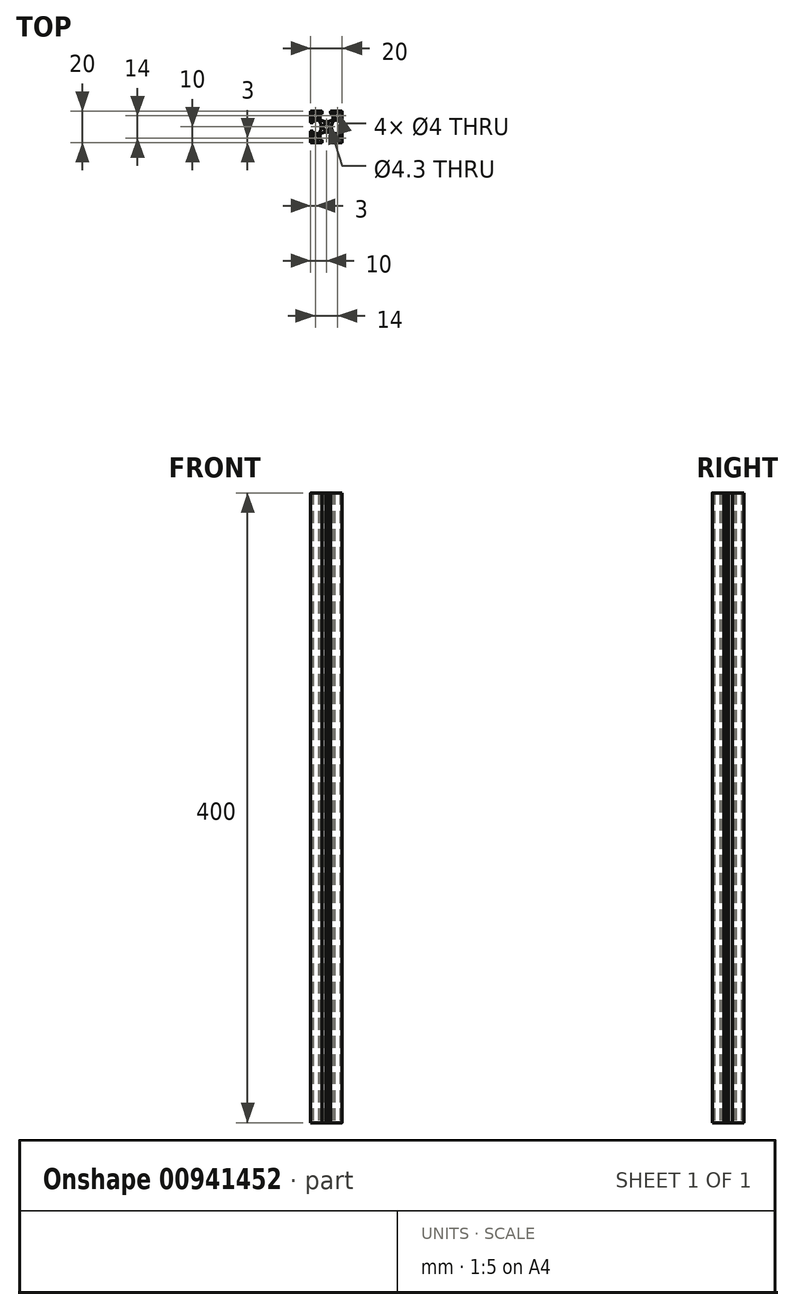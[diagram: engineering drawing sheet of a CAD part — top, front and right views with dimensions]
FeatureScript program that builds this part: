
annotation { "Feature Type Name" : "Feature", "Feature Type Description" : "" }
export const myFeature = defineFeature(function(context is Context, id is Id, definition is map)
    precondition{}
    {
        {
            var Q0;
            Q0=qCreatedBy(makeId("Top.planeOp"),FACE);
            var sketch = newSketch(context, id + "F0", { "sketchPlane" : qUnion([Q0])});
            skLineSegment(sketch, "E0", {"start": v(-11.2, 0) * mm, "end": v(11.2, 0) * mm});
            skCircle(sketch, "E1", {"center": v(0, 0) * mm, "radius": 2.15 * mm});
            skLineSegment(sketch, "E2", {"start": v(4.15, 4.94) * mm, "end": v(4.15, 8.2) * mm});
            skArc(sketch, "E3", {"start": v(4.15, 8.2) * mm, "mid": v(4.06, 8.41) * mm, "end": v(3.85, 8.5) * mm});
            skLineSegment(sketch, "E4", {"start": v(3.85, 8.5) * mm, "end": v(2.95, 8.5) * mm});
            skArc(sketch, "E5", {"start": v(2.95, 8.5) * mm, "mid": v(2.74, 8.59) * mm, "end": v(2.65, 8.8) * mm});
            skLineSegment(sketch, "E6", {"start": v(2.65, 8.8) * mm, "end": v(2.65, 9.7) * mm});
            skArc(sketch, "E7", {"start": v(2.65, 9.7) * mm, "mid": v(2.74, 9.91) * mm, "end": v(2.95, 10) * mm});
            skLineSegment(sketch, "E8", {"start": v(2.95, 10) * mm, "end": v(9.7, 10) * mm});
            skArc(sketch, "E9", {"start": v(9.7, 10) * mm, "mid": v(9.91, 9.91) * mm, "end": v(10, 9.7) * mm});
            skLineSegment(sketch, "E10", {"start": v(10, 9.7) * mm, "end": v(10, 2.95) * mm});
            skArc(sketch, "E11", {"start": v(10, 2.95) * mm, "mid": v(9.91, 2.74) * mm, "end": v(9.7, 2.65) * mm});
            skLineSegment(sketch, "E12", {"start": v(9.7, 2.65) * mm, "end": v(8.8, 2.65) * mm});
            skArc(sketch, "E13", {"start": v(8.8, 2.65) * mm, "mid": v(8.59, 2.74) * mm, "end": v(8.5, 2.95) * mm});
            skLineSegment(sketch, "E14", {"start": v(8.5, 2.95) * mm, "end": v(8.5, 3.85) * mm});
            skArc(sketch, "E15", {"start": v(8.5, 3.85) * mm, "mid": v(8.41, 4.06) * mm, "end": v(8.2, 4.15) * mm});
            skLineSegment(sketch, "E16", {"start": v(8.2, 4.15) * mm, "end": v(4.94, 4.15) * mm});
            skArc(sketch, "E17", {"start": v(4.94, 4.15) * mm, "mid": v(4.81, 4.12) * mm, "end": v(4.7, 4.04) * mm});
            skArc(sketch, "E18", {"start": v(4.7, 4.04) * mm, "mid": v(3.71, 2.28) * mm, "end": v(3.3, 0.3) * mm});
            skLineSegment(sketch, "E19", {"start": v(3.3, 0.3) * mm, "end": v(3, 0) * mm});
            skLineSegment(sketch, "E20", {"start": v(3, 0) * mm, "end": v(3.3, -0.3) * mm});
            skArc(sketch, "E21", {"start": v(3.3, -0.3) * mm, "mid": v(3.71, -2.28) * mm, "end": v(4.7, -4.04) * mm});
            skArc(sketch, "E22", {"start": v(4.7, -4.04) * mm, "mid": v(4.81, -4.12) * mm, "end": v(4.94, -4.15) * mm});
            skLineSegment(sketch, "E23", {"start": v(4.94, -4.15) * mm, "end": v(8.2, -4.15) * mm});
            skArc(sketch, "E24", {"start": v(8.2, -4.15) * mm, "mid": v(8.41, -4.06) * mm, "end": v(8.5, -3.85) * mm});
            skLineSegment(sketch, "E25", {"start": v(8.5, -3.85) * mm, "end": v(8.5, -2.95) * mm});
            skArc(sketch, "E26", {"start": v(8.5, -2.95) * mm, "mid": v(8.59, -2.74) * mm, "end": v(8.8, -2.65) * mm});
            skLineSegment(sketch, "E27", {"start": v(8.8, -2.65) * mm, "end": v(9.7, -2.65) * mm});
            skArc(sketch, "E28", {"start": v(9.7, -2.65) * mm, "mid": v(9.91, -2.74) * mm, "end": v(10, -2.95) * mm});
            skLineSegment(sketch, "E29", {"start": v(10, -2.95) * mm, "end": v(10, -9.7) * mm});
            skArc(sketch, "E30", {"start": v(10, -9.7) * mm, "mid": v(9.91, -9.91) * mm, "end": v(9.7, -10) * mm});
            skLineSegment(sketch, "E31", {"start": v(9.7, -10) * mm, "end": v(2.95, -10) * mm});
            skArc(sketch, "E32", {"start": v(2.95, -10) * mm, "mid": v(2.74, -9.91) * mm, "end": v(2.65, -9.7) * mm});
            skLineSegment(sketch, "E33", {"start": v(2.65, -9.7) * mm, "end": v(2.65, -8.8) * mm});
            skArc(sketch, "E34", {"start": v(2.65, -8.8) * mm, "mid": v(2.74, -8.59) * mm, "end": v(2.95, -8.5) * mm});
            skLineSegment(sketch, "E35", {"start": v(2.95, -8.5) * mm, "end": v(3.85, -8.5) * mm});
            skArc(sketch, "E36", {"start": v(3.85, -8.5) * mm, "mid": v(4.06, -8.41) * mm, "end": v(4.15, -8.2) * mm});
            skLineSegment(sketch, "E37", {"start": v(4.15, -8.2) * mm, "end": v(4.15, -4.94) * mm});
            skArc(sketch, "E38", {"start": v(4.15, -4.94) * mm, "mid": v(4.12, -4.81) * mm, "end": v(4.04, -4.7) * mm});
            skArc(sketch, "E39", {"start": v(4.04, -4.7) * mm, "mid": v(2.28, -3.71) * mm, "end": v(0.3, -3.3) * mm});
            skLineSegment(sketch, "E40", {"start": v(0.3, -3.3) * mm, "end": v(0, -3) * mm});
            skLineSegment(sketch, "E41", {"start": v(0, -3) * mm, "end": v(-0.3, -3.3) * mm});
            skArc(sketch, "E42", {"start": v(-0.3, -3.3) * mm, "mid": v(-2.28, -3.71) * mm, "end": v(-4.04, -4.7) * mm});
            skArc(sketch, "E43", {"start": v(-4.04, -4.7) * mm, "mid": v(-4.12, -4.81) * mm, "end": v(-4.15, -4.94) * mm});
            skLineSegment(sketch, "E44", {"start": v(-4.15, -4.94) * mm, "end": v(-4.15, -8.2) * mm});
            skArc(sketch, "E45", {"start": v(-4.15, -8.2) * mm, "mid": v(-4.06, -8.41) * mm, "end": v(-3.85, -8.5) * mm});
            skLineSegment(sketch, "E46", {"start": v(-3.85, -8.5) * mm, "end": v(-2.95, -8.5) * mm});
            skArc(sketch, "E47", {"start": v(-2.95, -8.5) * mm, "mid": v(-2.74, -8.59) * mm, "end": v(-2.65, -8.8) * mm});
            skLineSegment(sketch, "E48", {"start": v(-2.65, -8.8) * mm, "end": v(-2.65, -9.7) * mm});
            skArc(sketch, "E49", {"start": v(-2.65, -9.7) * mm, "mid": v(-2.74, -9.91) * mm, "end": v(-2.95, -10) * mm});
            skLineSegment(sketch, "E50", {"start": v(-2.95, -10) * mm, "end": v(-9.7, -10) * mm});
            skArc(sketch, "E51", {"start": v(-9.7, -10) * mm, "mid": v(-9.91, -9.91) * mm, "end": v(-10, -9.7) * mm});
            skLineSegment(sketch, "E52", {"start": v(-10, -9.7) * mm, "end": v(-10, -2.95) * mm});
            skArc(sketch, "E53", {"start": v(-10, -2.95) * mm, "mid": v(-9.91, -2.74) * mm, "end": v(-9.7, -2.65) * mm});
            skLineSegment(sketch, "E54", {"start": v(-9.7, -2.65) * mm, "end": v(-8.8, -2.65) * mm});
            skArc(sketch, "E55", {"start": v(-8.8, -2.65) * mm, "mid": v(-8.59, -2.74) * mm, "end": v(-8.5, -2.95) * mm});
            skLineSegment(sketch, "E56", {"start": v(-8.5, -2.95) * mm, "end": v(-8.5, -3.85) * mm});
            skArc(sketch, "E57", {"start": v(-8.5, -3.85) * mm, "mid": v(-8.41, -4.06) * mm, "end": v(-8.2, -4.15) * mm});
            skLineSegment(sketch, "E58", {"start": v(-8.2, -4.15) * mm, "end": v(-4.94, -4.15) * mm});
            skArc(sketch, "E59", {"start": v(-4.94, -4.15) * mm, "mid": v(-4.81, -4.12) * mm, "end": v(-4.7, -4.04) * mm});
            skArc(sketch, "E60", {"start": v(-4.7, -4.04) * mm, "mid": v(-3.71, -2.28) * mm, "end": v(-3.3, -0.3) * mm});
            skLineSegment(sketch, "E61", {"start": v(-3.3, -0.3) * mm, "end": v(-3, 0) * mm});
            skLineSegment(sketch, "E62", {"start": v(-3, 0) * mm, "end": v(-3.3, 0.3) * mm});
            skArc(sketch, "E63", {"start": v(-3.3, 0.3) * mm, "mid": v(-3.71, 2.28) * mm, "end": v(-4.7, 4.04) * mm});
            skArc(sketch, "E64", {"start": v(-4.7, 4.04) * mm, "mid": v(-4.81, 4.12) * mm, "end": v(-4.94, 4.15) * mm});
            skLineSegment(sketch, "E65", {"start": v(-4.94, 4.15) * mm, "end": v(-8.2, 4.15) * mm});
            skArc(sketch, "E66", {"start": v(-8.2, 4.15) * mm, "mid": v(-8.41, 4.06) * mm, "end": v(-8.5, 3.85) * mm});
            skLineSegment(sketch, "E67", {"start": v(-8.5, 3.85) * mm, "end": v(-8.5, 2.95) * mm});
            skArc(sketch, "E68", {"start": v(-8.5, 2.95) * mm, "mid": v(-8.59, 2.74) * mm, "end": v(-8.8, 2.65) * mm});
            skLineSegment(sketch, "E69", {"start": v(-8.8, 2.65) * mm, "end": v(-9.7, 2.65) * mm});
            skArc(sketch, "E70", {"start": v(-9.7, 2.65) * mm, "mid": v(-9.91, 2.74) * mm, "end": v(-10, 2.95) * mm});
            skLineSegment(sketch, "E71", {"start": v(-10, 2.95) * mm, "end": v(-10, 9.7) * mm});
            skArc(sketch, "E72", {"start": v(-10, 9.7) * mm, "mid": v(-9.91, 9.91) * mm, "end": v(-9.7, 10) * mm});
            skLineSegment(sketch, "E73", {"start": v(-9.7, 10) * mm, "end": v(-2.95, 10) * mm});
            skArc(sketch, "E74", {"start": v(-2.95, 10) * mm, "mid": v(-2.74, 9.91) * mm, "end": v(-2.65, 9.7) * mm});
            skLineSegment(sketch, "E75", {"start": v(-2.65, 9.7) * mm, "end": v(-2.65, 8.8) * mm});
            skArc(sketch, "E76", {"start": v(-2.65, 8.8) * mm, "mid": v(-2.74, 8.59) * mm, "end": v(-2.95, 8.5) * mm});
            skLineSegment(sketch, "E77", {"start": v(-2.95, 8.5) * mm, "end": v(-3.85, 8.5) * mm});
            skArc(sketch, "E78", {"start": v(-3.85, 8.5) * mm, "mid": v(-4.06, 8.41) * mm, "end": v(-4.15, 8.2) * mm});
            skLineSegment(sketch, "E79", {"start": v(-4.15, 8.2) * mm, "end": v(-4.15, 4.94) * mm});
            skArc(sketch, "E80", {"start": v(-4.15, 4.94) * mm, "mid": v(-4.12, 4.81) * mm, "end": v(-4.04, 4.7) * mm});
            skArc(sketch, "E81", {"start": v(-4.04, 4.7) * mm, "mid": v(-2.28, 3.71) * mm, "end": v(-0.3, 3.3) * mm});
            skLineSegment(sketch, "E82", {"start": v(-0.3, 3.3) * mm, "end": v(0, 3) * mm});
            skLineSegment(sketch, "E83", {"start": v(0, 3) * mm, "end": v(0.3, 3.3) * mm});
            skArc(sketch, "E84", {"start": v(0.3, 3.3) * mm, "mid": v(2.28, 3.71) * mm, "end": v(4.04, 4.7) * mm});
            skArc(sketch, "E85", {"start": v(4.04, 4.7) * mm, "mid": v(4.12, 4.81) * mm, "end": v(4.15, 4.94) * mm});
            skLineSegment(sketch, "E86", {"start": v(-9.5, 7) * mm, "end": v(-4.5, 7) * mm});
            skLineSegment(sketch, "E87", {"start": v(-7, 9.5) * mm, "end": v(-7, 4.5) * mm});
            skCircle(sketch, "E88", {"center": v(-7, 7) * mm, "radius": 2 * mm});
            skLineSegment(sketch, "E89", {"start": v(-9.5, -7) * mm, "end": v(-4.5, -7) * mm});
            skLineSegment(sketch, "E90", {"start": v(-7, -9.5) * mm, "end": v(-7, -4.5) * mm});
            skCircle(sketch, "E91", {"center": v(-7, -7) * mm, "radius": 2 * mm});
            skLineSegment(sketch, "E92", {"start": v(0, 11.2) * mm, "end": v(0, -11.2) * mm});
            skLineSegment(sketch, "E93", {"start": v(9.5, 7) * mm, "end": v(4.5, 7) * mm});
            skLineSegment(sketch, "E94", {"start": v(7, 9.5) * mm, "end": v(7, 4.5) * mm});
            skCircle(sketch, "E95", {"center": v(7, 7) * mm, "radius": 2 * mm});
            skCircle(sketch, "E96", {"center": v(7, -7) * mm, "radius": 2 * mm});
            skLineSegment(sketch, "E97", {"start": v(7, -9.5) * mm, "end": v(7, -4.5) * mm});
            skLineSegment(sketch, "E98", {"start": v(9.5, -7) * mm, "end": v(4.5, -7) * mm});
            skSolve(sketch);
        }
        {
            var Q0;
            Q0=makeQuery(id+"F0.imprint","IMPRINT",FACE,{"disambiguationData":[TD([[makeQuery(id+"F0.imprint","IMPRINT",EDGE,{"derivedFrom":sQuery(id+"F0.wireOp",EDGE,"E2")}),-1.0]])]});
            var Q1;
            {var subQ10=sQuery(id+"F0.wireOp",EDGE,"E20");Q1=makeQuery(id+"F0.imprint","IMPRINT",FACE,{"disambiguationData":[TD([[makeQuery(id+"F0.imprint","IMPRINT",EDGE,{"derivedFrom":subQ10}),-1.0]])]});}
            var Q2;
            {var subQ1=sQuery(id+"F0.wireOp",EDGE,"E41");Q2=makeQuery(id+"F0.imprint","IMPRINT",FACE,{"disambiguationData":[TD([[makeQuery(id+"F0.imprint","IMPRINT",EDGE,{"derivedFrom":subQ1}),-1.0]])]});}
            var Q3;
            {var subQ0=sQuery(id+"F0.wireOp",EDGE,"E62");Q3=makeQuery(id+"F0.imprint","IMPRINT",FACE,{"disambiguationData":[TD([[makeQuery(id+"F0.imprint","IMPRINT",EDGE,{"derivedFrom":subQ0}),-1.0]])]});}
            extrude(context, id + "F1", {"entities" : qUnion([Q0, Q1, Q2, Q3]), "depth" : 400 * mm, "offsetDistance" : 25 * mm});
        }
    });
